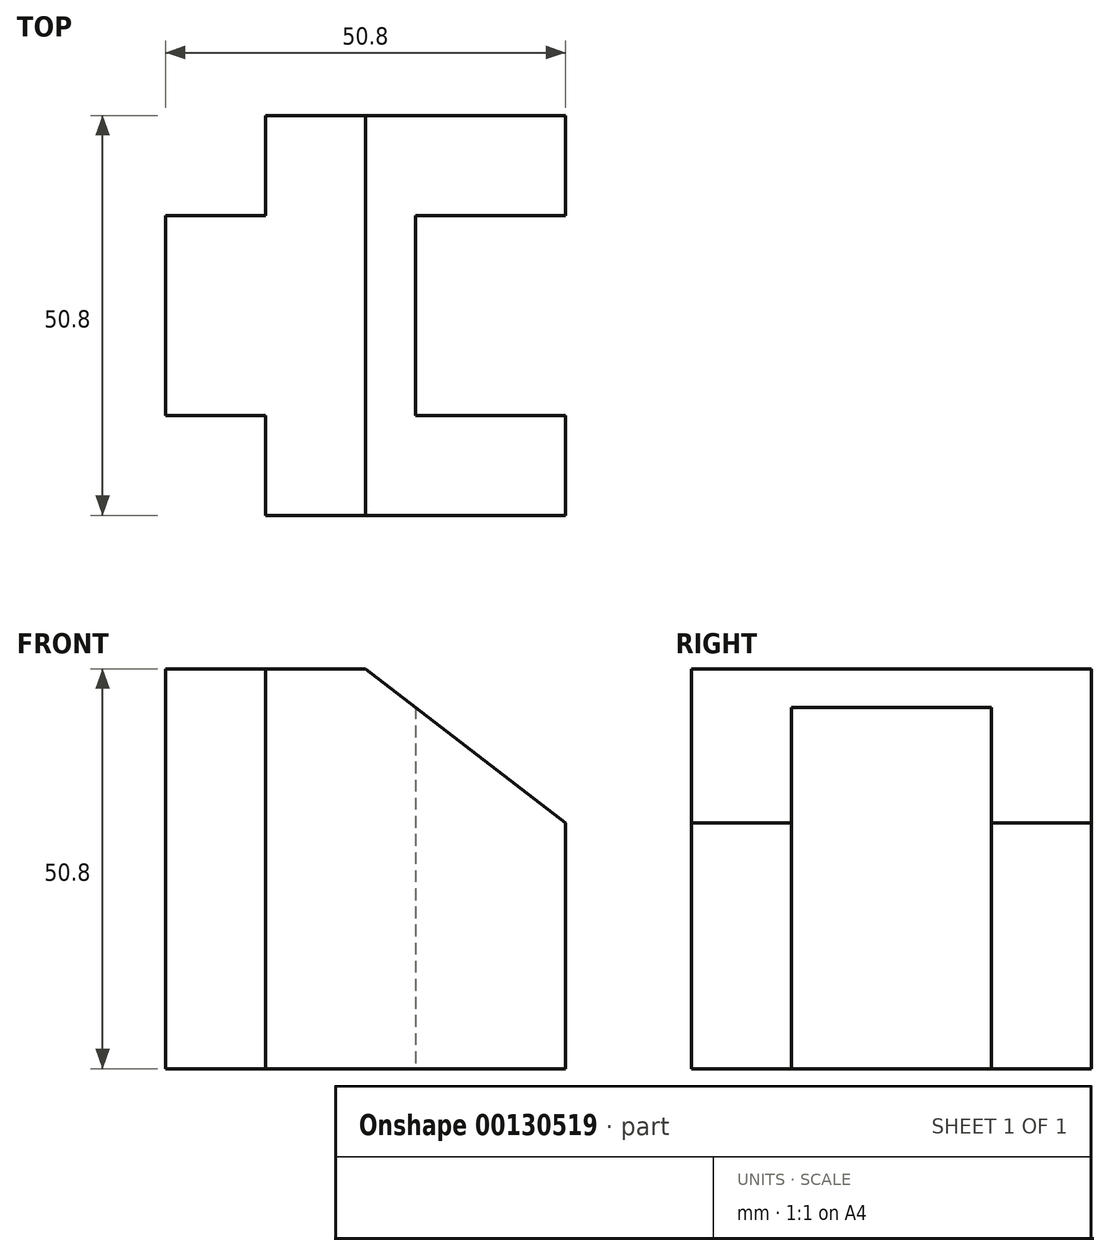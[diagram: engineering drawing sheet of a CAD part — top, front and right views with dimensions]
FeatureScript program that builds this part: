
annotation { "Feature Type Name" : "Feature", "Feature Type Description" : "" }
export const myFeature = defineFeature(function(context is Context, id is Id, definition is map)
    precondition{}
    {
        {
            var Q0;
            Q0=qCreatedBy(makeId("Front.planeOp"),FACE);
            var sketch = newSketch(context, id + "F0", { "sketchPlane" : qUnion([Q0])});
            skLineSegment(sketch, "E0", {"start": v(0, 50.8) * mm, "end": v(0, 0) * mm});
            skLineSegment(sketch, "E1", {"start": v(0, 0) * mm, "end": v(50.8, 0) * mm});
            skLineSegment(sketch, "E2", {"start": v(50.8, 0) * mm, "end": v(50.8, 31.21) * mm});
            skLineSegment(sketch, "E3", {"start": v(50.8, 31.21) * mm, "end": v(25.4, 50.8) * mm});
            skLineSegment(sketch, "E4", {"start": v(25.4, 50.8) * mm, "end": v(0, 50.8) * mm});
            skSolve(sketch);
        }
        {
            var Q0;
            Q0 = qSketchRegion(id + "F0", true);
            extrude(context, id + "F1", {"entities" : qUnion([Q0]), "depth" : 50.8 * mm});
        }
        {
            var Q0;
            Q0=makeQuery(id+"F1.opExtrude","SWEPT_FACE",FACE,{"disambiguationData":[OSD([sQuery(id+"F0.wireOp",EDGE,"E4")])]});
            var sketch = newSketch(context, id + "F2", { "sketchPlane" : qUnion([Q0])});
            skLineSegment(sketch, "E5", {"start": v(12.7, 0) * mm, "end": v(12.7, -12.7) * mm});
            skLineSegment(sketch, "E6", {"start": v(12.7, -12.7) * mm, "end": v(0, -12.7) * mm});
            skLineSegment(sketch, "E7", {"start": v(0, -12.7) * mm, "end": v(0, 0) * mm});
            skLineSegment(sketch, "E8", {"start": v(0, 0) * mm, "end": v(12.7, 0) * mm});
            skLineSegment(sketch, "E9", {"start": v(12.7, -50.8) * mm, "end": v(12.7, -38.1) * mm});
            skLineSegment(sketch, "E10", {"start": v(12.7, -38.1) * mm, "end": v(0, -38.1) * mm});
            skLineSegment(sketch, "E11", {"start": v(0, -38.1) * mm, "end": v(0, -50.8) * mm});
            skLineSegment(sketch, "E12", {"start": v(0, -50.8) * mm, "end": v(12.7, -50.8) * mm});
            skSolve(sketch);
        }
        {
            var Q0;
            Q0 = qSketchRegion(id + "F2", true);
            extrude(context, id + "F3", {"entities" : qUnion([Q0]), "operationType" : NewBodyOperationType.REMOVE, "endBound" : BoundingType.THROUGH_ALL, "oppositeDirection" : true, "depth" : 25.4 * mm});
        }
        {
            var Q0;
            Q0=makeQuery(id+"F1.opExtrude","SWEPT_FACE",FACE,{"disambiguationData":[OSD([sQuery(id+"F0.wireOp",EDGE,"E1")])]});
            var sketch = newSketch(context, id + "F4", { "sketchPlane" : qUnion([Q0])});
            skLineSegment(sketch, "E13", {"start": v(50.8, 38.1) * mm, "end": v(50.8, 12.7) * mm});
            skPoint(sketch, "E13.startSnap0", {"position": v(50.8, 25.4) * mm});
            skLineSegment(sketch, "E14", {"start": v(50.8, 12.7) * mm, "end": v(31.75, 12.7) * mm});
            skLineSegment(sketch, "E15", {"start": v(31.75, 12.7) * mm, "end": v(31.75, 38.1) * mm});
            skLineSegment(sketch, "E16", {"start": v(31.75, 38.1) * mm, "end": v(50.8, 38.1) * mm});
            skSolve(sketch);
        }
        {
            var Q0;
            Q0 = qSketchRegion(id + "F4", true);
            extrude(context, id + "F5", {"entities" : qUnion([Q0]), "operationType" : NewBodyOperationType.REMOVE, "endBound" : BoundingType.THROUGH_ALL, "oppositeDirection" : true, "depth" : 25.4 * mm});
        }
    });
